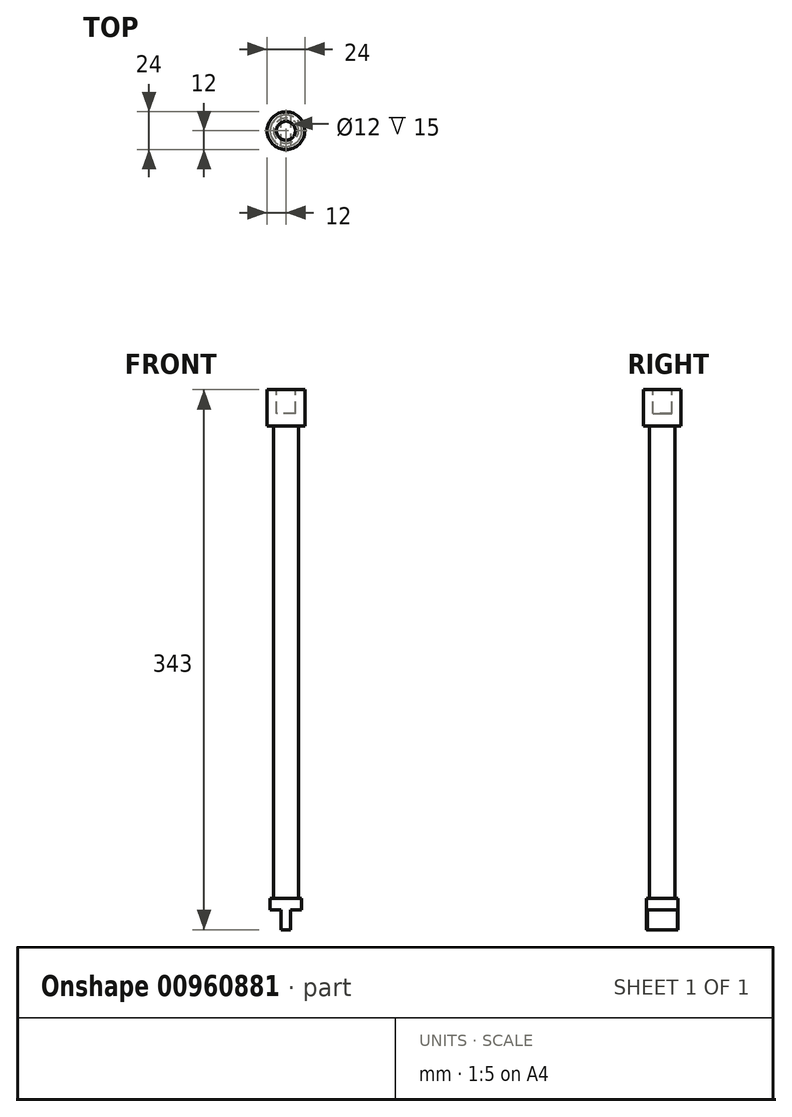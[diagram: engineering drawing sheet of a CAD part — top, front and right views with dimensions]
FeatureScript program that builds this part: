
annotation { "Feature Type Name" : "Feature", "Feature Type Description" : "" }
export const myFeature = defineFeature(function(context is Context, id is Id, definition is map)
    precondition{}
    {
        {
            var Q0;
            Q0=qCreatedBy(makeId("Front.planeOp"),FACE);
            var sketch = newSketch(context, id + "F0", { "sketchPlane" : qUnion([Q0])});
            skLineSegment(sketch, "E0", {"start": v(0, 286.39) * mm, "end": v(12, 286.39) * mm});
            skLineSegment(sketch, "E1", {"start": v(12, 286.39) * mm, "end": v(12, 263.39) * mm});
            skLineSegment(sketch, "E2", {"start": v(12, 263.39) * mm, "end": v(8, 263.39) * mm});
            skLineSegment(sketch, "E3", {"start": v(8, 263.39) * mm, "end": v(8, -36.61) * mm});
            skLineSegment(sketch, "E4", {"start": v(8, -36.61) * mm, "end": v(10, -36.61) * mm});
            skLineSegment(sketch, "E5", {"start": v(10, -36.61) * mm, "end": v(10, -56.61) * mm});
            skLineSegment(sketch, "E6", {"start": v(10, -56.61) * mm, "end": v(0, -56.61) * mm});
            skLineSegment(sketch, "E7", {"start": v(0, -56.61) * mm, "end": v(0, 286.39) * mm});
            skSolve(sketch);
        }
        {
            var Q0;
            Q0 = qSketchRegion(id + "F0", true);
            var Q1;
            Q1=sQuery(id+"F0.wireOp",EDGE,"E7");
            revolve(context, id + "F1", {"surfaceOperationType" : NewSurfaceOperationType.NEW, "entities" : qUnion([Q0]), "axis" : qUnion([Q1]), "revolveType" : RevolveType.FULL});
        }
        {
            var Q0;
            Q0=makeQuery(id+"F1.opRevolve","SWEPT_FACE",FACE,{"disambiguationData":[OSD([sQuery(id+"F0.wireOp",EDGE,"E6")])]});
            var sketch = newSketch(context, id + "F2", { "sketchPlane" : qUnion([Q0])});
            skLineSegment(sketch, "E8", {"start": v(0, 0) * mm, "end": v(3, 0) * mm});
            skLineSegment(sketch, "E9", {"start": v(3, 0) * mm, "end": v(-3, 0) * mm});
            skLineSegment(sketch, "E10", {"start": v(-3, 0) * mm, "end": v(-3, 9.54) * mm});
            skLineSegment(sketch, "E11", {"start": v(-3, 9.54) * mm, "end": v(-3, -9.54) * mm});
            skLineSegment(sketch, "E12", {"start": v(3, 0) * mm, "end": v(3, 9.54) * mm});
            skLineSegment(sketch, "E13", {"start": v(3, 9.54) * mm, "end": v(3, -9.54) * mm});
            skSolve(sketch);
        }
        {
            var Q0;
            Q0 = qSketchRegion(id + "F2", true);
            var Q1;
            {var subQ0=sQuery(id+"F2.wireOp",EDGE,"E13");var subQ1=makeQuery(id+"F2.imprint","INTERSECT",VERTEX,{"derivedFrom":[sQuery(id+"F2.wireOp",EDGE,"E9"),subQ0]});Q1=makeQuery(id+"F2.imprint","IMPRINT",FACE,{"disambiguationData":[TD([[makeQuery(id+"F2.imprint","IMPRINT",EDGE,{"disambiguationData":[TD([[subQ1,1.0]])],"derivedFrom":subQ0}),1.0]])]});}
            var Q2;
            {var subQ0=sQuery(id+"F2.wireOp",EDGE,"E11");var subQ1=makeQuery(id+"F2.imprint","INTERSECT",VERTEX,{"derivedFrom":[sQuery(id+"F2.wireOp",EDGE,"E9"),subQ0]});Q2=makeQuery(id+"F2.imprint","IMPRINT",FACE,{"disambiguationData":[TD([[makeQuery(id+"F2.imprint","IMPRINT",EDGE,{"disambiguationData":[TD([[subQ1,1.0]])],"derivedFrom":subQ0}),-1.0]])]});}
            extrude(context, id + "F3", {"entities" : qUnion([Q0, Q1, Q2]), "operationType" : NewBodyOperationType.REMOVE, "oppositeDirection" : true, "depth" : 12.75 * mm, "offsetDistance" : 25 * mm});
        }
        {
            var Q0;
            Q0=makeQuery(id+"F1.opRevolve","SWEPT_FACE",FACE,{"disambiguationData":[OSD([sQuery(id+"F0.wireOp",EDGE,"E0")])]});
            var sketch = newSketch(context, id + "F4", { "sketchPlane" : qUnion([Q0])});
            skCircle(sketch, "E14", {"center": v(0, 0) * mm, "radius": 6 * mm});
            skSolve(sketch);
        }
        {
            var Q0;
            Q0=makeQuery(id+"F4.imprint","IMPRINT",FACE,{"disambiguationData":[TD([[makeQuery(id+"F4.imprint","IMPRINT",EDGE,{"derivedFrom":sQuery(id+"F4.wireOp",EDGE,"E14")}),1.0]])]});
            extrude(context, id + "F5", {"entities" : qUnion([Q0]), "operationType" : NewBodyOperationType.REMOVE, "oppositeDirection" : true, "depth" : 15 * mm, "offsetDistance" : 25 * mm});
        }
    });
